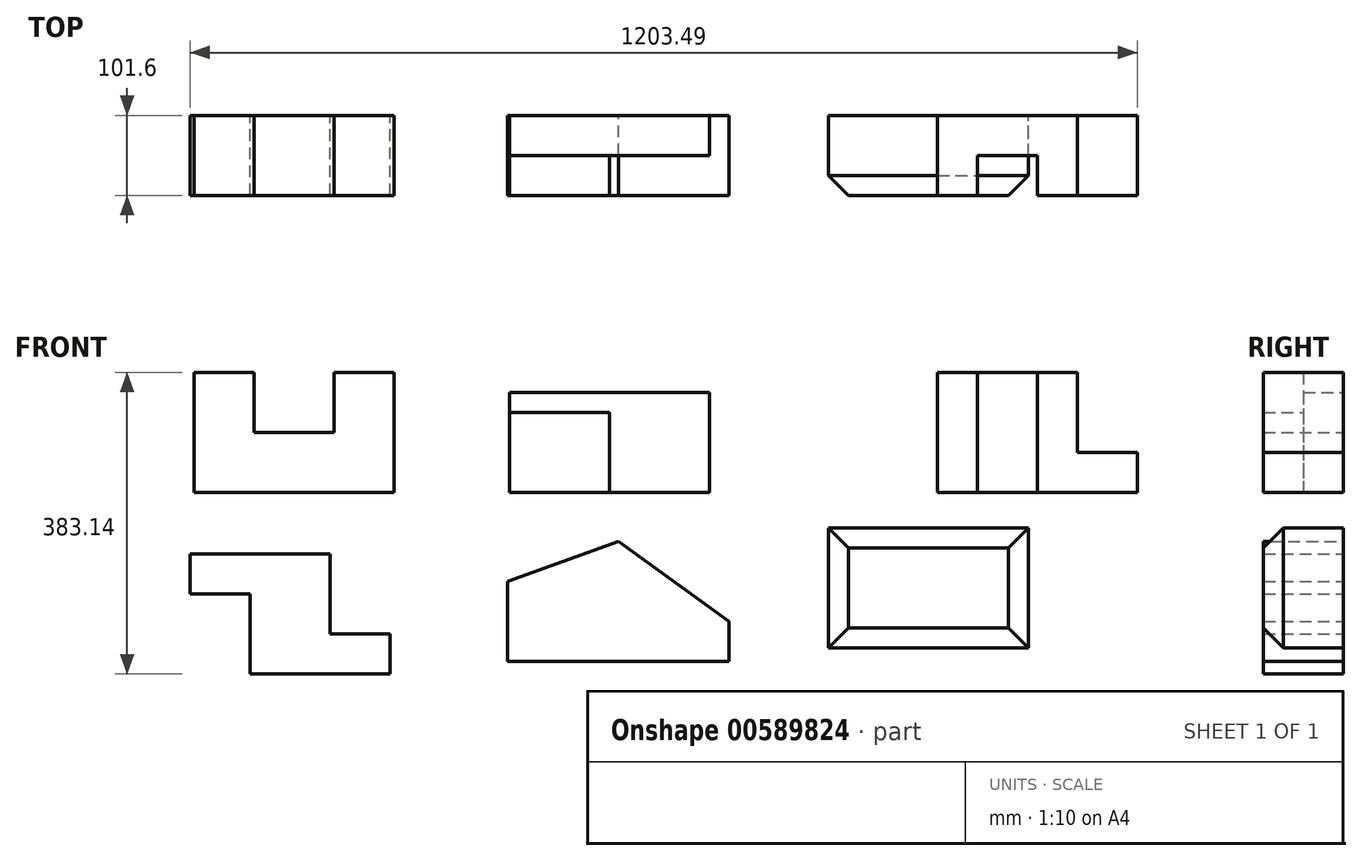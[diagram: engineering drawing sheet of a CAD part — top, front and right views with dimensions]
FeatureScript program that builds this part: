
annotation { "Feature Type Name" : "Feature", "Feature Type Description" : "" }
export const myFeature = defineFeature(function(context is Context, id is Id, definition is map)
    precondition{}
    {
        {
            var Q0;
            Q0=qCreatedBy(makeId("Front.planeOp"),FACE);
            var sketch = newSketch(context, id + "F0", { "sketchPlane" : qUnion([Q0])});
            skLineSegment(sketch, "E0", {"start": v(0, 0) * mm, "end": v(254, 0) * mm});
            skLineSegment(sketch, "E1", {"start": v(254, 0) * mm, "end": v(254, 152.4) * mm});
            skLineSegment(sketch, "E2", {"start": v(0, 152.4) * mm, "end": v(0, 0) * mm});
            skLineSegment(sketch, "E3", {"start": v(0, 152.4) * mm, "end": v(76.2, 152.4) * mm});
            skLineSegment(sketch, "E4", {"start": v(76.2, 152.4) * mm, "end": v(76.2, 76.2) * mm});
            skLineSegment(sketch, "E5", {"start": v(76.2, 76.2) * mm, "end": v(177.8, 76.2) * mm});
            skLineSegment(sketch, "E6", {"start": v(177.8, 76.2) * mm, "end": v(177.8, 152.4) * mm});
            skLineSegment(sketch, "E7", {"start": v(254, 152.4) * mm, "end": v(177.8, 152.4) * mm});
            skSolve(sketch);
        }
        {
            var Q0;
            Q0 = qSketchRegion(id + "F0", true);
            extrude(context, id + "F1", {"entities" : qUnion([Q0]), "depth" : 101.6 * mm, "offsetDistance" : 25.4 * mm});
        }
        {
            var Q0;
            Q0=qCreatedBy(makeId("Front.planeOp"),FACE);
            var sketch = newSketch(context, id + "F2", { "sketchPlane" : qUnion([Q0])});
            skLineSegment(sketch, "E8", {"start": v(400.86, 127) * mm, "end": v(654.86, 127) * mm});
            skLineSegment(sketch, "E9", {"start": v(654.86, 127) * mm, "end": v(654.86, 0) * mm});
            skLineSegment(sketch, "E10", {"start": v(400.86, 0) * mm, "end": v(400.86, 101.6) * mm});
            skLineSegment(sketch, "E11", {"start": v(400.86, 101.6) * mm, "end": v(527.86, 101.6) * mm});
            skLineSegment(sketch, "E12", {"start": v(527.86, 101.6) * mm, "end": v(527.86, 0) * mm});
            skPoint(sketch, "E12.endSnap0", {"position": v(527.86, 0) * mm});
            skLineSegment(sketch, "E13", {"start": v(400.86, 127) * mm, "end": v(400.86, 101.6) * mm});
            skLineSegment(sketch, "E14", {"start": v(400.86, 0) * mm, "end": v(527.86, 0) * mm});
            skLineSegment(sketch, "E15", {"start": v(527.86, 0) * mm, "end": v(654.86, 0) * mm});
            skSolve(sketch);
        }
        {
            var Q0;
            Q0=qCreatedBy(makeId("Front.planeOp"),FACE);
            var sketch = newSketch(context, id + "F3", { "sketchPlane" : qUnion([Q0])});
            skLineSegment(sketch, "E16", {"start": v(944.4, 0) * mm, "end": v(1198.4, 0) * mm});
            skLineSegment(sketch, "E17", {"start": v(944.4, 152.4) * mm, "end": v(944.4, 0) * mm});
            skLineSegment(sketch, "E18", {"start": v(944.4, 152.4) * mm, "end": v(1122.2, 152.4) * mm});
            skLineSegment(sketch, "E19", {"start": v(1122.2, 152.4) * mm, "end": v(1122.2, 50.8) * mm});
            skLineSegment(sketch, "E20", {"start": v(1122.2, 50.8) * mm, "end": v(1198.4, 50.8) * mm});
            skLineSegment(sketch, "E21", {"start": v(944.4, 152.4) * mm, "end": v(995.2, 152.4) * mm});
            skLineSegment(sketch, "E22", {"start": v(995.2, 152.4) * mm, "end": v(995.2, 0) * mm});
            skLineSegment(sketch, "E23", {"start": v(1122.2, 152.4) * mm, "end": v(1071.4, 152.4) * mm});
            skLineSegment(sketch, "E24", {"start": v(1071.4, 152.4) * mm, "end": v(1071.4, 0) * mm});
            skLineSegment(sketch, "E25", {"start": v(1198.4, 0) * mm, "end": v(1198.4, 50.8) * mm});
            skSolve(sketch);
        }
        {
            var Q0;
            Q0=makeQuery(id+"F2.imprint","IMPRINT",FACE,{"disambiguationData":[TD([[makeQuery(id+"F2.imprint","IMPRINT",EDGE,{"derivedFrom":sQuery(id+"F2.wireOp",EDGE,"E8")}),-1.0]])]});
            extrude(context, id + "F4", {"entities" : qUnion([Q0]), "depth" : 50.8 * mm, "offsetDistance" : 25.4 * mm});
        }
        {
            var Q0;
            Q0=makeQuery(id+"F2.imprint","IMPRINT",FACE,{"disambiguationData":[TD([[makeQuery(id+"F2.imprint","IMPRINT",EDGE,{"derivedFrom":sQuery(id+"F2.wireOp",EDGE,"E10")}),-1.0]])]});
            extrude(context, id + "F5", {"entities" : qUnion([Q0]), "operationType" : NewBodyOperationType.ADD, "depth" : 101.6 * mm, "offsetDistance" : 25.4 * mm});
        }
        {
            var Q0;
            {var subQ0=sQuery(id+"F3.wireOp",EDGE,"E17");Q0=makeQuery(id+"F3.imprint","IMPRINT",FACE,{"disambiguationData":[TD([[makeQuery(id+"F3.imprint","IMPRINT",EDGE,{"derivedFrom":subQ0}),1.0]])]});}
            extrude(context, id + "F6", {"entities" : qUnion([Q0]), "depth" : 101.6 * mm, "offsetDistance" : 25.4 * mm});
        }
        {
            var Q0;
            Q0 = qSketchRegion(id + "F3", true);
            extrude(context, id + "F7", {"entities" : qUnion([Q0]), "operationType" : NewBodyOperationType.ADD, "depth" : 25.4 * mm, "offsetDistance" : 25.4 * mm});
        }
        {
            var Q0;
            Q0=makeQuery(id+"F3.imprint","IMPRINT",FACE,{"disambiguationData":[TD([[makeQuery(id+"F3.imprint","IMPRINT",EDGE,{"derivedFrom":sQuery(id+"F3.wireOp",EDGE,"E18")}),-1.0]])]});
            extrude(context, id + "F8", {"entities" : qUnion([Q0]), "operationType" : NewBodyOperationType.ADD, "depth" : 50.8 * mm, "offsetDistance" : 25.4 * mm});
        }
        {
            var Q0;
            Q0=makeQuery(id+"F7.opExtrude","CAP_FACE",FACE,{"disambiguationData":[OSD([sQuery(id+"F3.wireOp",EDGE,"E16"),sQuery(id+"F3.wireOp",EDGE,"E17"),sQuery(id+"F3.wireOp",EDGE,"E18"),sQuery(id+"F3.wireOp",EDGE,"E19"),sQuery(id+"F3.wireOp",EDGE,"E20"),sQuery(id+"F3.wireOp",EDGE,"E21"),sQuery(id+"F3.wireOp",EDGE,"E23"),sQuery(id+"F3.wireOp",EDGE,"E25")])],"isStart":false});
            extrude(context, id + "F9", {"entities" : qUnion([Q0]), "operationType" : NewBodyOperationType.ADD, "depth" : 76.2 * mm, "offsetDistance" : 25.4 * mm});
        }
        {
            var Q0;
            Q0=qCreatedBy(makeId("Front.planeOp"),FACE);
            var sketch = newSketch(context, id + "F10", { "sketchPlane" : qUnion([Q0])});
            skLineSegment(sketch, "E26", {"start": v(-5.1, -78.34) * mm, "end": v(172.7, -78.34) * mm});
            skLineSegment(sketch, "E27", {"start": v(172.7, -78.34) * mm, "end": v(172.7, -179.94) * mm});
            skLineSegment(sketch, "E28", {"start": v(172.7, -179.94) * mm, "end": v(248.9, -179.94) * mm});
            skLineSegment(sketch, "E29", {"start": v(-5.1, -78.34) * mm, "end": v(-5.1, -129.14) * mm});
            skLineSegment(sketch, "E30", {"start": v(-5.1, -129.14) * mm, "end": v(71.1, -129.14) * mm});
            skLineSegment(sketch, "E31", {"start": v(71.1, -129.14) * mm, "end": v(71.1, -230.74) * mm});
            skLineSegment(sketch, "E32", {"start": v(71.1, -230.74) * mm, "end": v(248.9, -230.74) * mm});
            skLineSegment(sketch, "E33", {"start": v(248.9, -230.74) * mm, "end": v(248.9, -179.94) * mm});
            skSolve(sketch);
        }
        {
            var Q0;
            Q0 = qSketchRegion(id + "F10", true);
            extrude(context, id + "F11", {"entities" : qUnion([Q0]), "depth" : 101.6 * mm, "offsetDistance" : 25.4 * mm});
        }
        {
            var Q0;
            Q0=qCreatedBy(makeId("Front.planeOp"),FACE);
            var sketch = newSketch(context, id + "F12", { "sketchPlane" : qUnion([Q0])});
            skLineSegment(sketch, "E34", {"start": v(398.31, -112.8) * mm, "end": v(398.31, -214.4) * mm});
            skLineSegment(sketch, "E35", {"start": v(398.31, -214.4) * mm, "end": v(679.8, -214.4) * mm});
            skLineSegment(sketch, "E36", {"start": v(679.8, -214.4) * mm, "end": v(679.8, -163.6) * mm});
            skLineSegment(sketch, "E37", {"start": v(398.31, -112.8) * mm, "end": v(539.06, -62) * mm});
            skPoint(sketch, "E37.endSnap0", {"position": v(539.06, -214.4) * mm});
            skLineSegment(sketch, "E38", {"start": v(539.06, -62) * mm, "end": v(679.8, -163.6) * mm});
            skSolve(sketch);
        }
        {
            var Q0;
            Q0 = qSketchRegion(id + "F12", true);
            extrude(context, id + "F13", {"entities" : qUnion([Q0]), "depth" : 101.6 * mm, "offsetDistance" : 25.4 * mm});
        }
        {
            var Q0;
            Q0=qCreatedBy(makeId("Front.planeOp"),FACE);
            var sketch = newSketch(context, id + "F14", { "sketchPlane" : qUnion([Q0])});
            skLineSegment(sketch, "E39", {"start": v(806.07, -45.11) * mm, "end": v(806.07, -197.51) * mm});
            skLineSegment(sketch, "E40", {"start": v(806.07, -197.51) * mm, "end": v(1060.07, -197.51) * mm});
            skLineSegment(sketch, "E41", {"start": v(1060.07, -197.51) * mm, "end": v(1060.07, -45.11) * mm});
            skLineSegment(sketch, "E42", {"start": v(1060.07, -45.11) * mm, "end": v(806.07, -45.11) * mm});
            skSolve(sketch);
        }
        {
            var Q0;
            Q0 = qSketchRegion(id + "F14", true);
            extrude(context, id + "F15", {"entities" : qUnion([Q0]), "depth" : 101.6 * mm, "offsetDistance" : 25.4 * mm});
        }
        {
            var Q0;
            Q0=makeQuery(id+"F15.opExtrude","CAP_FACE",FACE,{"disambiguationData":[OSD([sQuery(id+"F14.wireOp",EDGE,"E39"),sQuery(id+"F14.wireOp",EDGE,"E40"),sQuery(id+"F14.wireOp",EDGE,"E41"),sQuery(id+"F14.wireOp",EDGE,"E42")])],"isStart":false});
            chamfer(context, id + "F16", {"entities" : qUnion([Q0]), "width" : 25.4 * mm, "tangentPropagation" : true});
        }
    });
